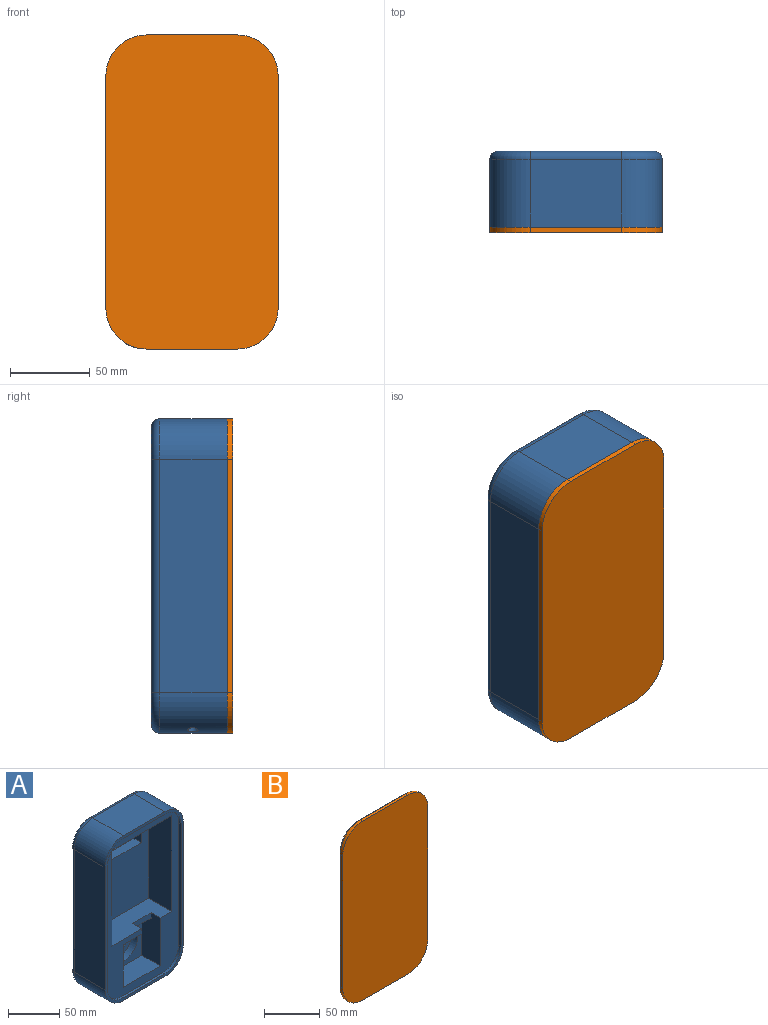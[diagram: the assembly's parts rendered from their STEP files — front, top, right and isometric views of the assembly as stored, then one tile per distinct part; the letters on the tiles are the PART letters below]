
ASSEMBLY  parts=2 mates=1
PART A: 54 faces, bbox 112.1x47.6x201 mm
  f0: plane 190.5x101.6mm, normal (0,-1,0), area 6753.4mm2, adj f1,f2,f3,f10,f11,f17,f18,f19
  f1: plane 50.8x25.4mm, normal (0,0,-1), area 967.7mm2, adj f0,f17,f19,f20,f52,f53
  f2: plane 114.3x31.75mm, normal (1,0,0), area 3489.3mm2, adj f0,f3,f11,f12,f50,f51
  f3: plane 82.55x31.75mm, normal (0,0,1), area 2196.5mm2, adj f0,f2,f10,f12,f19,f50,f52,f53
  f4: cylinder r=3.17mm len=18.24mm, axis (0,0,-1), area 340.5mm2, adj f26,f49
  f5: plane 146.05x42.55mm, normal (1,0,0), area 6213.7mm2, adj f24,f27,f34,f48
  f6: plane 57.15x42.55mm, normal (0,0,1), area 2431.4mm2, adj f24,f25,f33,f48
  f7: plane 146.05x42.55mm, normal (-1,0,0), area 6213.7mm2, adj f25,f26,f29,f48
  f8: plane 57.15x42.55mm, normal (0,0,-1), area 2431.4mm2, adj f26,f27,f30,f48
  f9: plane 186.69x97.79mm, normal (0,1,0), area 15181.7mm2, adj f23,f28,f29,f30,f31,f32,f33,f34
  f10: plane 114.3x31.75mm, normal (-1,0,0), area 3629mm2, adj f0,f3,f11,f12
  f11: plane 82.55x31.75mm, normal (0,0,-1), area 2621mm2, adj f0,f2,f10,f12
  f12: plane 114.3x82.55mm, normal (0,-1,0), area 7764.6mm2, adj f2,f3,f10,f11,f13,f14,f15,f16
  f13: plane 26.99x10.16mm, normal (1,0,0), area 274.2mm2, adj f12,f14,f16,f39
  f14: plane 61.91x10.16mm, normal (0,0,1), area 629mm2, adj f12,f13,f15,f38
  f15: plane 26.99x10.16mm, normal (-1,0,0), area 274.2mm2, adj f12,f14,f16,f36
  f16: plane 61.91x10.16mm, normal (0,0,-1), area 629mm2, adj f12,f13,f15,f37
  f17: plane 50.8x25.4mm, normal (1,0,0), area 1290.3mm2, adj f0,f1,f18,f20
  f18: plane 50.8x25.4mm, normal (0,0,1), area 1290.3mm2, adj f0,f17,f19,f20
  f19: plane 57.15x25.4mm, normal (-1,0,0), area 1371mm2, adj f0,f1,f3,f18,f20,f53
  f20: plane 50.8x50.8mm, normal (0,-1,0), area 1343.6mm2, adj f1,f17,f18,f19,f21
  f21: cylinder r=19.84mm len=39.69mm, axis (0,-1,0), area 989.7mm2, adj f20,f22
  f22: plane 39.69x39.69mm, normal (0,-1,0), area 665.1mm2, adj f21,f23
  f23: cylinder r=13.49mm len=26.99mm, axis (0,-1,0), area 942.2mm2, adj f9,f22
  f24: cylinder r=25.4mm len=42.55mm, axis (0,-1,0), area 1697.5mm2, adj f5,f6,f35,f48
  f25: cylinder r=25.4mm len=42.55mm, axis (0,1,0), area 1697.5mm2, adj f6,f7,f31,f48
  f26: cylinder r=25.4mm len=42.55mm, axis (0,-1,0), area 1663.2mm2, adj f4,f7,f8,f28,f48
  f27: cylinder r=25.4mm len=42.55mm, axis (0,1,0), area 1697.5mm2, adj f5,f8,f32,f48
  f28: torus R=20.32mm, axis (0,-1,0), area 295.2mm2, adj f9,f26,f29,f30
  f29: cylinder r=5.08mm len=146.05mm, axis (0,0,-1), area 1165.4mm2, adj f7,f9,f28,f31
  f30: cylinder r=5.08mm len=57.15mm, axis (1,0,0), area 456mm2, adj f8,f9,f28,f32
  f31: torus R=20.32mm, axis (0,-1,0), area 295.2mm2, adj f9,f25,f29,f33
  f32: torus R=20.32mm, axis (0,-1,0), area 295.2mm2, adj f9,f27,f30,f34
  f33: cylinder r=5.08mm len=57.15mm, axis (-1,0,0), area 456mm2, adj f6,f9,f31,f35
  f34: cylinder r=5.08mm len=146.05mm, axis (0,0,1), area 1165.4mm2, adj f5,f9,f32,f35
  f35: torus R=20.32mm, axis (0,-1,0), area 295.2mm2, adj f9,f24,f33,f34
  f36: cylinder r=2.54mm len=32.07mm, axis (0,0,1), area 115mm2, adj f9,f15,f37,f38
  f37: cylinder r=2.54mm len=66.99mm, axis (-1,0,0), area 254.4mm2, adj f9,f16,f36,f39
  f38: cylinder r=2.54mm len=66.99mm, axis (1,0,0), area 254.4mm2, adj f9,f14,f36,f39
  f39: cylinder r=2.54mm len=32.07mm, axis (0,0,-1), area 115mm2, adj f9,f13,f37,f38
  f40: cylinder r=22.23mm len=22.23mm, axis (0,1,0), area 110.8mm2, adj f0,f41,f47,f48
  f41: plane 57.15x3.18mm, normal (0,0,1), area 181.5mm2, adj f0,f40,f42,f48
  f42: cylinder r=22.23mm len=22.23mm, axis (0,1,0), area 110.8mm2, adj f0,f41,f43,f48
  f43: plane 146.05x3.18mm, normal (1,0,0), area 463.7mm2, adj f0,f42,f44,f48
  f44: cylinder r=22.23mm len=22.23mm, axis (0,1,0), area 110.8mm2, adj f0,f43,f45,f48
  f45: plane 57.15x3.18mm, normal (0,0,-1), area 181.5mm2, adj f0,f44,f46,f48
  f46: cylinder r=22.23mm len=22.23mm, axis (0,1,0), area 110.8mm2, adj f0,f45,f47,f48
  f47: plane 146.05x3.18mm, normal (-1,0,0), area 463.7mm2, adj f0,f40,f46,f48
  f48: plane 196.85x107.95mm, normal (0,-1,0), area 1765.4mm2, adj f5,f6,f7,f8,f24,f25,f26,f27
  f49: plane 12.7x12.7mm, normal (0,0,1), area 95mm2, adj f4,f50
  f50: cylinder r=6.35mm len=63.5mm, axis (0,0,1), area 2195.7mm2, adj f2,f3,f49,f51
  f51: plane 11x3.18mm, normal (0,0,-1), area 24.8mm2, adj f2,f50
  f52: plane 12.7x6.35mm, normal (1,0,0), area 80.6mm2, adj f0,f1,f3,f53
  f53: plane 25.4x6.35mm, normal (0,-1,0), area 161.3mm2, adj f1,f3,f19,f52
PART B: 19 faces, bbox 108x6.4x196.9 mm
  f0: plane 57.15x3.18mm, normal (0,0,-1), area 181.5mm2, adj f1,f7,f8,f9
  f1: cylinder r=22.23mm len=22.23mm, axis (0,1,0), area 110.8mm2, adj f0,f2,f8,f9
  f2: plane 146.05x3.18mm, normal (1,0,0), area 463.7mm2, adj f1,f3,f8,f9
  f3: cylinder r=22.23mm len=22.23mm, axis (0,1,0), area 110.8mm2, adj f2,f4,f8,f9
  f4: plane 57.15x3.18mm, normal (0,0,1), area 181.5mm2, adj f3,f5,f8,f9
  f5: cylinder r=22.23mm len=22.23mm, axis (0,1,0), area 110.8mm2, adj f4,f6,f8,f9
  f6: plane 146.05x3.18mm, normal (-1,0,0), area 463.7mm2, adj f5,f7,f8,f9
  f7: cylinder r=22.23mm len=22.23mm, axis (0,1,0), area 110.8mm2, adj f0,f6,f8,f9
  f8: plane 190.5x101.6mm, normal (0,1,0), area 18930.8mm2, adj f0,f1,f2,f3,f4,f5,f6,f7
  f9: plane 196.85x107.95mm, normal (0,1,0), area 1765.4mm2, adj f0,f1,f2,f3,f4,f5,f6,f7
  f10: cylinder r=25.4mm len=25.4mm, axis (0,1,0), area 126.7mm2, adj f9,f11,f17,f18
  f11: plane 57.15x3.18mm, normal (0,0,1), area 181.5mm2, adj f9,f10,f12,f18
  f12: cylinder r=25.4mm len=25.4mm, axis (0,1,0), area 126.7mm2, adj f9,f11,f13,f18
  f13: plane 146.05x3.18mm, normal (-1,0,0), area 463.7mm2, adj f9,f12,f14,f18
  f14: cylinder r=25.4mm len=25.4mm, axis (0,1,0), area 126.7mm2, adj f9,f13,f15,f18
  f15: plane 57.15x3.18mm, normal (0,0,-1), area 181.5mm2, adj f9,f14,f16,f18
  f16: cylinder r=25.4mm len=25.4mm, axis (0,1,0), area 126.7mm2, adj f9,f15,f17,f18
  f17: plane 146.05x3.18mm, normal (1,0,0), area 463.7mm2, adj f9,f10,f16,f18
  f18: plane 196.85x107.95mm, normal (0,-1,0), area 20696.1mm2, adj f10,f11,f12,f13,f14,f15,f16,f17
PLACE A t=(-104.19,-22.76,-15.35)mm
PLACE B t=(-104.19,-67.21,-15.35)mm
MATE slider A.f25 <-> B.f5  axis (0,1,0) through (-132.76,-68.8,57.68)mm
